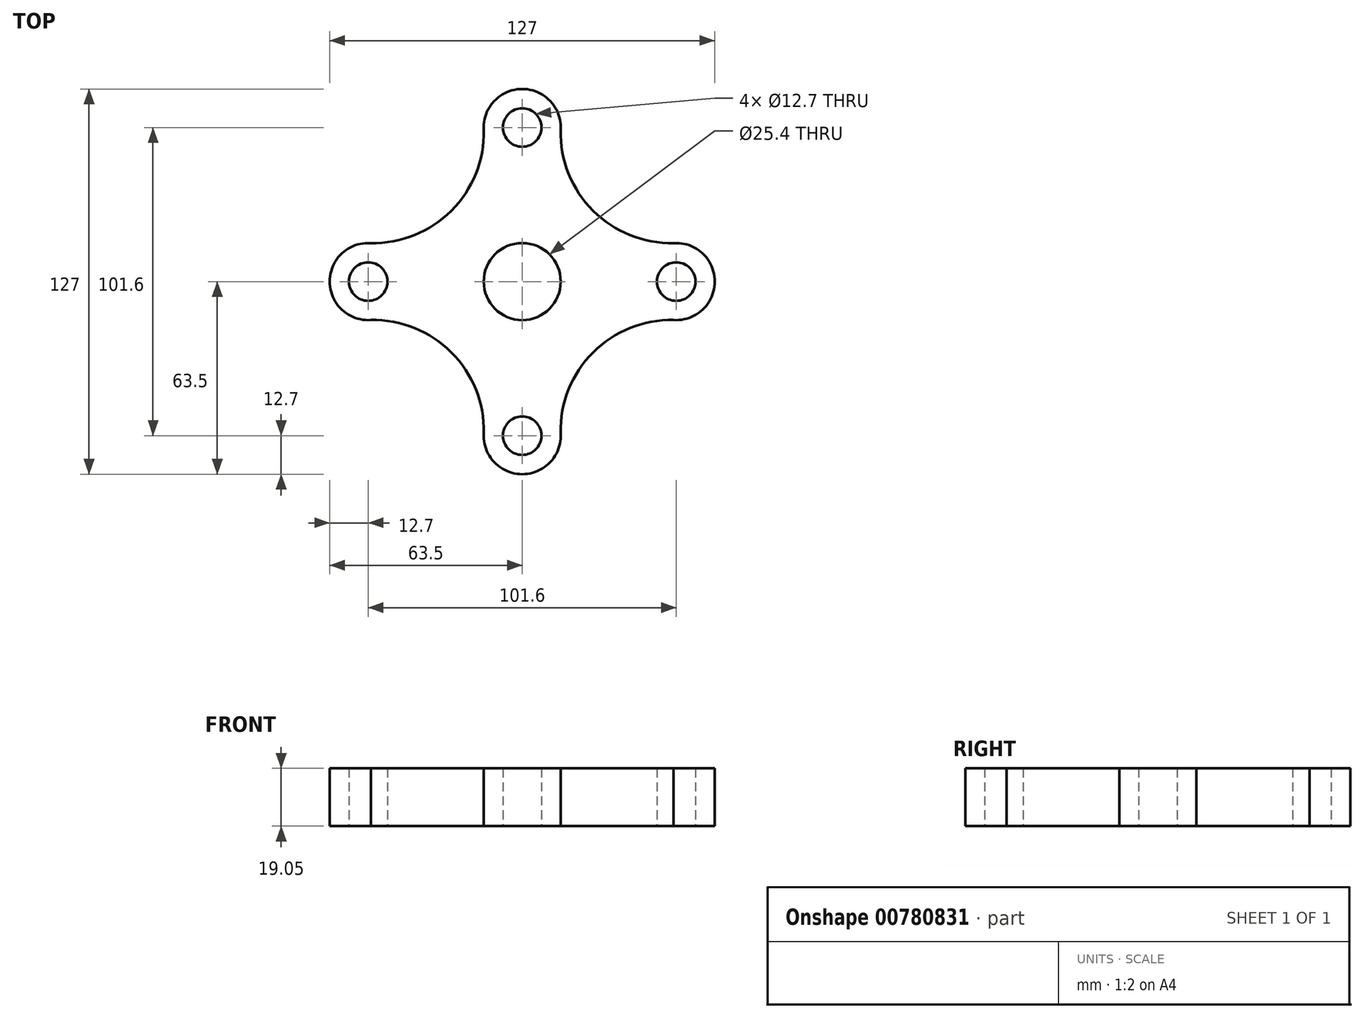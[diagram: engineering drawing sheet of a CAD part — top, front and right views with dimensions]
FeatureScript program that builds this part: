
annotation { "Feature Type Name" : "Feature", "Feature Type Description" : "" }
export const myFeature = defineFeature(function(context is Context, id is Id, definition is map)
    precondition{}
    {
        {
            var Q0;
            Q0=qCreatedBy(makeId("Top.planeOp"),FACE);
            var sketch = newSketch(context, id + "F0", { "sketchPlane" : qUnion([Q0])});
            skCircle(sketch, "E0", {"center": v(0, 0) * mm, "radius": 12.7 * mm});
            skCircle(sketch, "E1", {"center": v(0, 50.8) * mm, "radius": 6.35 * mm});
            skCircle(sketch, "E2", {"center": v(50.8, 0) * mm, "radius": 6.35 * mm});
            skCircle(sketch, "E3", {"center": v(0, -50.8) * mm, "radius": 6.35 * mm});
            skCircle(sketch, "E4", {"center": v(-50.8, 0) * mm, "radius": 6.35 * mm});
            skCircle(sketch, "E5", {"center": v(50.8, 0) * mm, "radius": 12.7 * mm});
            skCircle(sketch, "E6", {"center": v(0, 50.8) * mm, "radius": 12.7 * mm});
            skCircle(sketch, "E7", {"center": v(-50.8, 0) * mm, "radius": 12.7 * mm});
            skLineSegment(sketch, "E8", {"start": v(0, 50.8) * mm, "end": v(25, 50.8) * mm});
            skLineSegment(sketch, "E9", {"start": v(25, 50.8) * mm, "end": v(-22.05, 50.8) * mm});
            skLineSegment(sketch, "E10", {"start": v(50.8, 0) * mm, "end": v(50.8, 20.36) * mm});
            skLineSegment(sketch, "E11", {"start": v(50.8, 20.36) * mm, "end": v(50.8, -25.72) * mm});
            skLineSegment(sketch, "E12", {"start": v(0, -50.8) * mm, "end": v(40.9, -50.8) * mm});
            skLineSegment(sketch, "E13", {"start": v(40.9, -50.8) * mm, "end": v(-38.1, -50.8) * mm});
            skLineSegment(sketch, "E14", {"start": v(-50.8, 0) * mm, "end": v(-50.8, -20.9) * mm});
            skLineSegment(sketch, "E15", {"start": v(-50.8, -20.9) * mm, "end": v(-50.8, 23.58) * mm});
            skCircle(sketch, "E16", {"center": v(0, -50.8) * mm, "radius": 12.7 * mm});
            skArc(sketch, "E17", {"start": v(12.7, 50.8) * mm, "mid": v(23.36, 23.36) * mm, "end": v(50.8, 12.7) * mm});
            skArc(sketch, "E18", {"start": v(50.8, -12.7) * mm, "mid": v(23.36, -23.36) * mm, "end": v(12.7, -50.8) * mm});
            skArc(sketch, "E19", {"start": v(-12.7, -50.8) * mm, "mid": v(-23.36, -23.36) * mm, "end": v(-50.8, -12.7) * mm});
            skArc(sketch, "E20", {"start": v(-50.8, 12.7) * mm, "mid": v(-23.36, 23.36) * mm, "end": v(-12.7, 50.8) * mm});
            skSolve(sketch);
        }
        {
            var Q0;
            Q0 = qSketchRegion(id + "F0", true);
            extrude(context, id + "F1", {"entities" : qUnion([Q0]), "depth" : 19.05 * mm, "offsetDistance" : 25.4 * mm});
        }
    });
